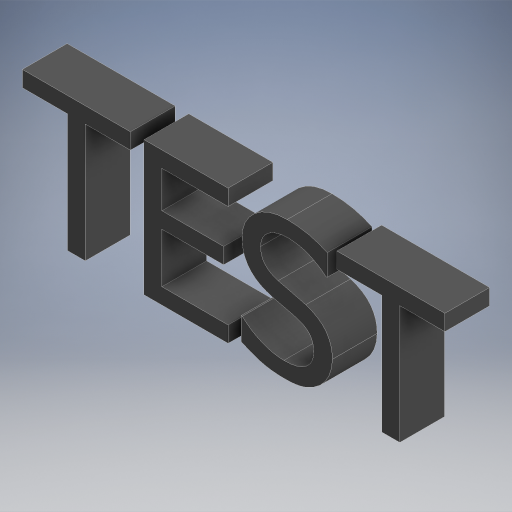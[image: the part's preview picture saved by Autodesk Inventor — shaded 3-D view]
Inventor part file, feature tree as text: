
AUTODESK INVENTOR PART (.ipt)
format: ipt  version: 2023.1 (Build 271208000, 208)  size: 483,840 bytes
history: native  units: in
note: dims shown in document units (in); Inventor stores cm internally (conversion verified against a paired STEP export)
features: extrude x1, sketch x1
ambient origin geometry x8: Origin, YZ Plane, XZ Plane, XY Plane, X Axis, Y Axis, Z Axis, Center Point
bodies: Solid1 (feature_tree)
feature tree (2):
  extrude  "Extrusion1"  [1 undecoded]
  sketch  "Sketch1"  dims[d0=1.0in d1=0.0in]
note: 1 required parameter value undecoded (feature->parameter linkage not recoverable at this tier; creation-order binding heuristic only, values carry confidence <= 0.55)
